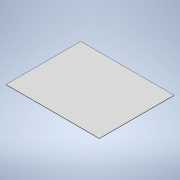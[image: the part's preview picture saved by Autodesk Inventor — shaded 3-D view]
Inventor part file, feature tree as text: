
AUTODESK INVENTOR PART (.ipt)
format: ipt  version: 2020 (Build 240168000, 168)  size: 91,136 bytes
history: native  units: mm
features: other x1, extrude x1, sketch x1
ambient origin geometry x8: Origin, YZ Plane, XZ Plane, XY Plane, X Axis, Y Axis, Z Axis, Center Point
bodies: Body1 (feature_tree)
feature tree (3):
  other  "Bryła1"
  extrude  "Wyciągnięcie proste1"  Depth=800.0mm
  sketch  "Szkic1"
